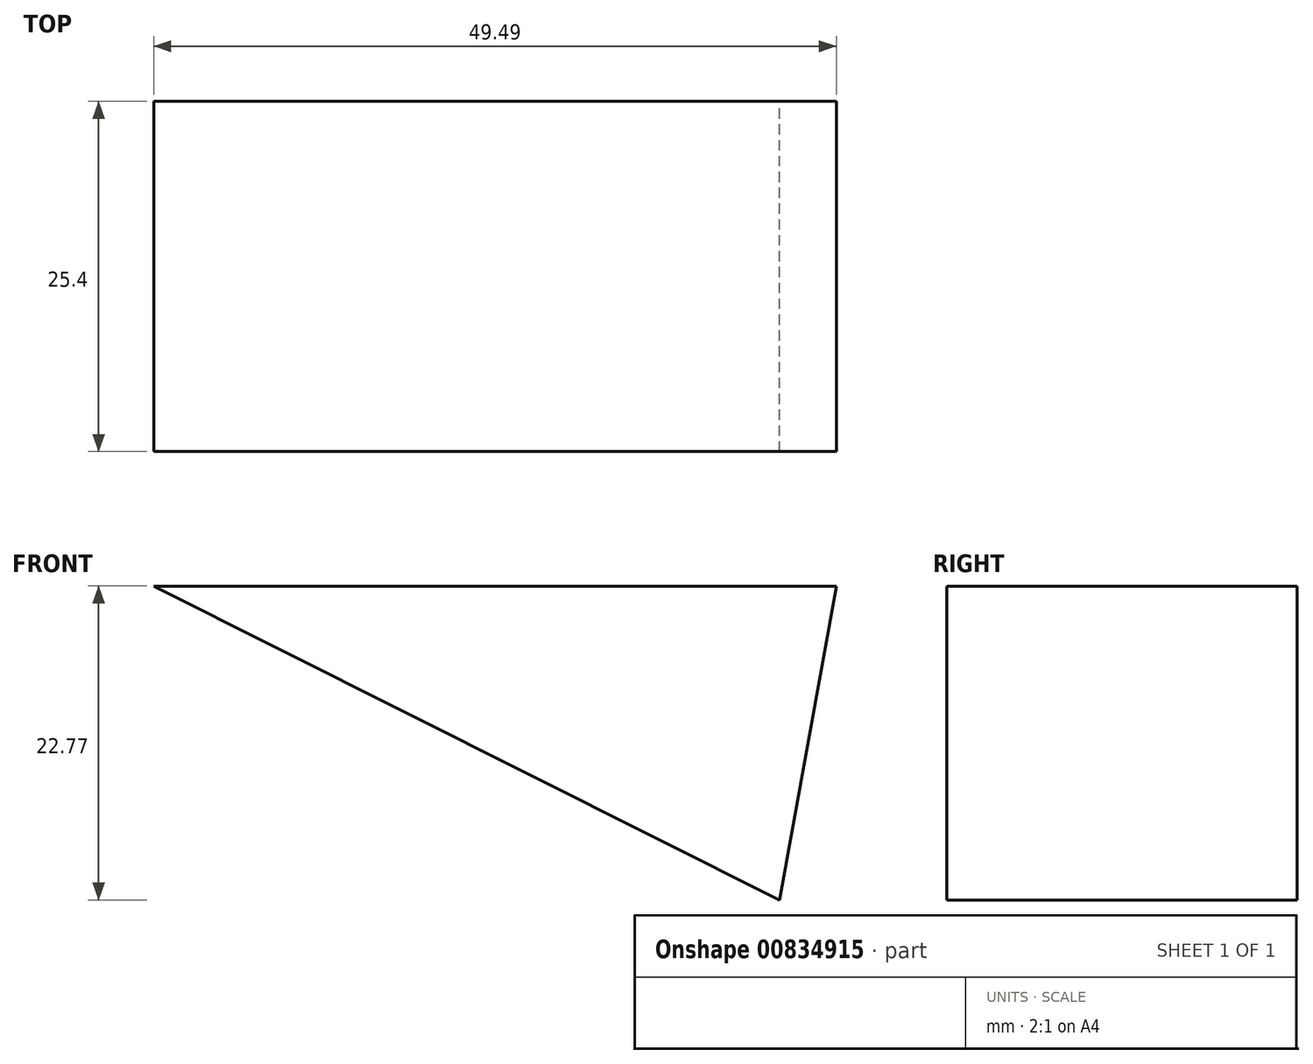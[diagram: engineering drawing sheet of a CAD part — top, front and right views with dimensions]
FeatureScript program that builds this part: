
annotation { "Feature Type Name" : "Feature", "Feature Type Description" : "" }
export const myFeature = defineFeature(function(context is Context, id is Id, definition is map)
    precondition{}
    {
        {
            var Q0;
            Q0=qCreatedBy(makeId("Front.planeOp"),FACE);
            var sketch = newSketch(context, id + "F0", { "sketchPlane" : qUnion([Q0])});
            skLineSegment(sketch, "E0", {"start": v(0, 0) * mm, "end": v(-45.37, 22.77) * mm});
            skLineSegment(sketch, "E1", {"start": v(-45.37, 22.77) * mm, "end": v(4.12, 22.77) * mm});
            skLineSegment(sketch, "E2", {"start": v(4.12, 22.77) * mm, "end": v(0, 0) * mm});
            skSolve(sketch);
        }
        {
            var Q0;
            Q0=makeQuery(id+"F0.imprint","IMPRINT",FACE,{"disambiguationData":[TD([[makeQuery(id+"F0.imprint","IMPRINT",EDGE,{"derivedFrom":sQuery(id+"F0.wireOp",EDGE,"E0")}),-1.0]])]});
            extrude(context, id + "F1", {"entities" : qUnion([Q0]), "depth" : 25.4 * mm, "offsetDistance" : 25.4 * mm});
        }
    });
